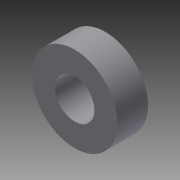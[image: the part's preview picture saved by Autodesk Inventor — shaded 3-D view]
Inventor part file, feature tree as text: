
AUTODESK INVENTOR PART (.ipt)
format: ipt  version: 2015 (Build 190159000, 159)  size: 78,848 bytes
history: native  units: in
note: dims shown in document units (in); Inventor stores cm internally (conversion verified against a paired STEP export)
features: extrude x1, sketch x1
ambient origin geometry x8: Origin, YZ Plane, XZ Plane, XY Plane, X Axis, Y Axis, Z Axis, Center Point
bodies: Solid1 (feature_tree)
feature tree (2):
  extrude  "Extrusion1"  Depth=0.2in
  sketch  "Sketch1"  dims[d0=0.257in d1=0.15in d2=0.2in d3=0.0in]
